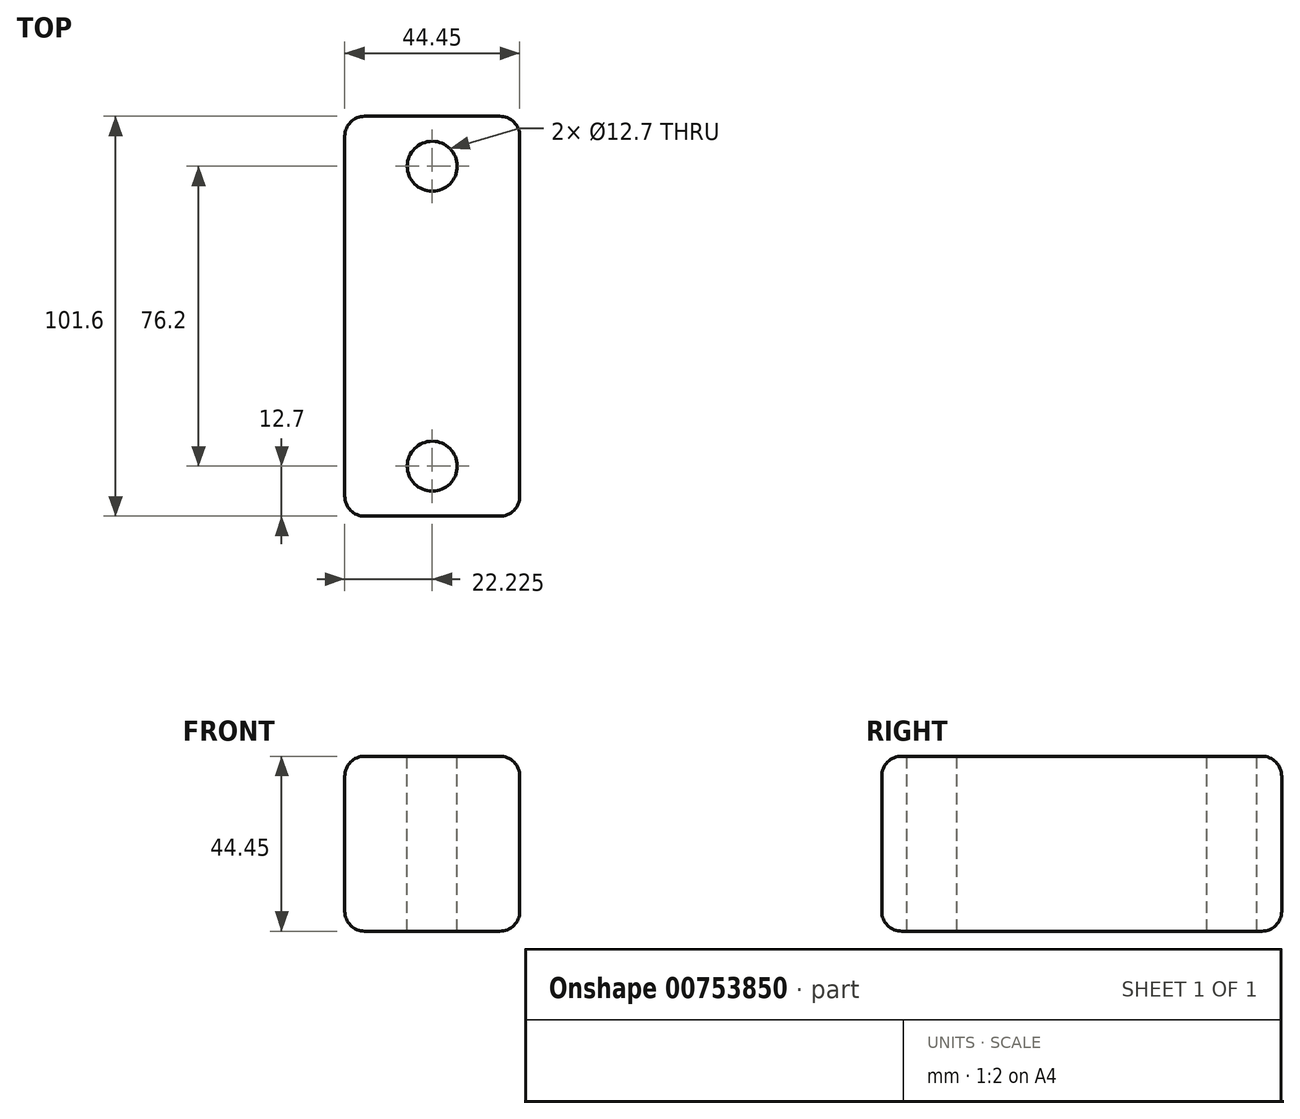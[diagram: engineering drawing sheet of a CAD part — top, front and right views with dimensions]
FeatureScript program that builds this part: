
annotation { "Feature Type Name" : "Feature", "Feature Type Description" : "" }
export const myFeature = defineFeature(function(context is Context, id is Id, definition is map)
    precondition{}
    {
        {
            var Q0;
            Q0=qCreatedBy(makeId("Top.planeOp"),FACE);
            var sketch = newSketch(context, id + "F0", { "sketchPlane" : qUnion([Q0])});
            skLineSegment(sketch, "E0.bottom", {"start": v(0, 0) * mm, "end": v(44.45, 0) * mm});
            skLineSegment(sketch, "E0.top", {"start": v(0, -101.6) * mm, "end": v(44.45, -101.6) * mm});
            skLineSegment(sketch, "E0.left", {"start": v(0, 0) * mm, "end": v(0, -101.6) * mm});
            skLineSegment(sketch, "E0.right", {"start": v(44.45, 0) * mm, "end": v(44.45, -101.6) * mm});
            skSolve(sketch);
        }
        {
            var Q0;
            Q0=makeQuery(id+"F0.imprint","IMPRINT",FACE,{"disambiguationData":[TD([[makeQuery(id+"F0.imprint","IMPRINT",EDGE,{"derivedFrom":sQuery(id+"F0.wireOp",EDGE,"E0.bottom")}),-1.0]])]});
            extrude(context, id + "F1", {"entities" : qUnion([Q0]), "depth" : 44.45 * mm, "offsetDistance" : 25.4 * mm});
        }
        {
            var Q0;
            Q0=makeQuery(id+"F1.opExtrude","CAP_FACE",FACE,{"disambiguationData":[OSD([sQuery(id+"F0.wireOp",EDGE,"E0.bottom"),sQuery(id+"F0.wireOp",EDGE,"E0.top"),sQuery(id+"F0.wireOp",EDGE,"E0.left"),sQuery(id+"F0.wireOp",EDGE,"E0.right")])],"isStart":false});
            var sketch = newSketch(context, id + "F2", { "sketchPlane" : qUnion([Q0])});
            skCircle(sketch, "E1", {"center": v(22.23, -12.7) * mm, "radius": 6.35 * mm});
            skCircle(sketch, "E2", {"center": v(22.23, -88.9) * mm, "radius": 6.35 * mm});
            skSolve(sketch);
        }
        {
            var Q0;
            Q0 = qSketchRegion(id + "F2", true);
            extrude(context, id + "F3", {"entities" : qUnion([Q0]), "operationType" : NewBodyOperationType.REMOVE, "oppositeDirection" : true, "depth" : 59.69 * mm, "offsetDistance" : 25.4 * mm});
        }
        {
            var Q0;
            Q0=makeQuery(id+"F1.opExtrude","CAP_EDGE",EDGE,{"disambiguationData":[OSD([sQuery(id+"F0.wireOp",EDGE,"E0.right")])],"isStart":false});
            var Q1;
            Q1=makeQuery(id+"F1.opExtrude","CAP_EDGE",EDGE,{"disambiguationData":[OSD([sQuery(id+"F0.wireOp",EDGE,"E0.right")])],"isStart":true});
            var Q2;
            Q2=makeQuery(id+"F1.opExtrude","CAP_EDGE",EDGE,{"disambiguationData":[OSD([sQuery(id+"F0.wireOp",EDGE,"E0.left")])],"isStart":true});
            var Q3;
            Q3=makeQuery(id+"F1.opExtrude","CAP_EDGE",EDGE,{"disambiguationData":[OSD([sQuery(id+"F0.wireOp",EDGE,"E0.left")])],"isStart":false});
            fillet(context, id + "F4", {"entities" : qUnion([Q0, Q1, Q2, Q3]), "radius" : 5.08 * mm, "tangentPropagation" : true, "allowEdgeOverflow" : false});
        }
        {
            var Q0;
            Q0=makeQuery(id+"F1.opExtrude","SWEPT_FACE",FACE,{"disambiguationData":[OSD([sQuery(id+"F0.wireOp",EDGE,"E0.bottom")])]});
            var Q1;
            Q1=makeQuery(id+"F1.opExtrude","SWEPT_FACE",FACE,{"disambiguationData":[OSD([sQuery(id+"F0.wireOp",EDGE,"E0.top")])]});
            fillet(context, id + "F5", {"entities" : qUnion([Q0, Q1]), "radius" : 5.08 * mm, "tangentPropagation" : true, "allowEdgeOverflow" : false});
        }
    });
